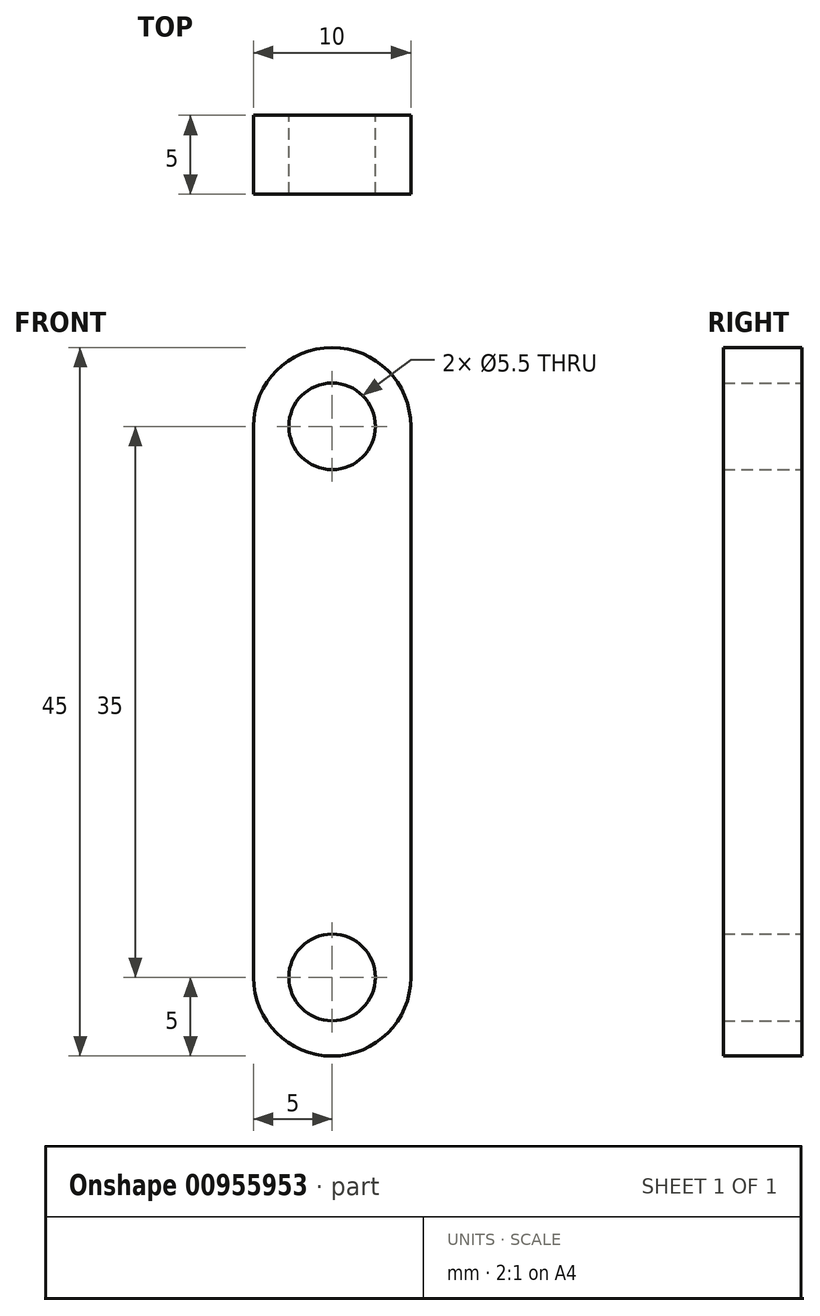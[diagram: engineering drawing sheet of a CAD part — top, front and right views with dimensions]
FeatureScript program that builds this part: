
annotation { "Feature Type Name" : "Feature", "Feature Type Description" : "" }
export const myFeature = defineFeature(function(context is Context, id is Id, definition is map)
    precondition{}
    {
        {
            var Q0;
            Q0=qCreatedBy(makeId("Front.planeOp"),FACE);
            var sketch = newSketch(context, id + "F0", { "sketchPlane" : qUnion([Q0])});
            skArc(sketch, "E0", {"start": v(5, 17.5) * mm, "mid": v(0, 22.5) * mm, "end": v(-5, 17.5) * mm});
            skArc(sketch, "E1.MirrorC", {"start": v(5, -17.5) * mm, "mid": v(0, -22.5) * mm, "end": v(-5, -17.5) * mm});
            skLineSegment(sketch, "E2", {"start": v(5, 17.5) * mm, "end": v(5, -17.5) * mm});
            skLineSegment(sketch, "E3", {"start": v(-5, -17.5) * mm, "end": v(-5, 17.5) * mm});
            skCircle(sketch, "E4", {"center": v(0, 17.5) * mm, "radius": 2.75 * mm});
            skCircle(sketch, "E5.MirrorC", {"center": v(0, -17.5) * mm, "radius": 2.75 * mm});
            skSolve(sketch);
        }
        {
            var Q0;
            Q0 = qSketchRegion(id + "F0", true);
            extrude(context, id + "F1", {"entities" : qUnion([Q0]), "depth" : 5 * mm, "offsetDistance" : 25 * mm});
        }
    });
